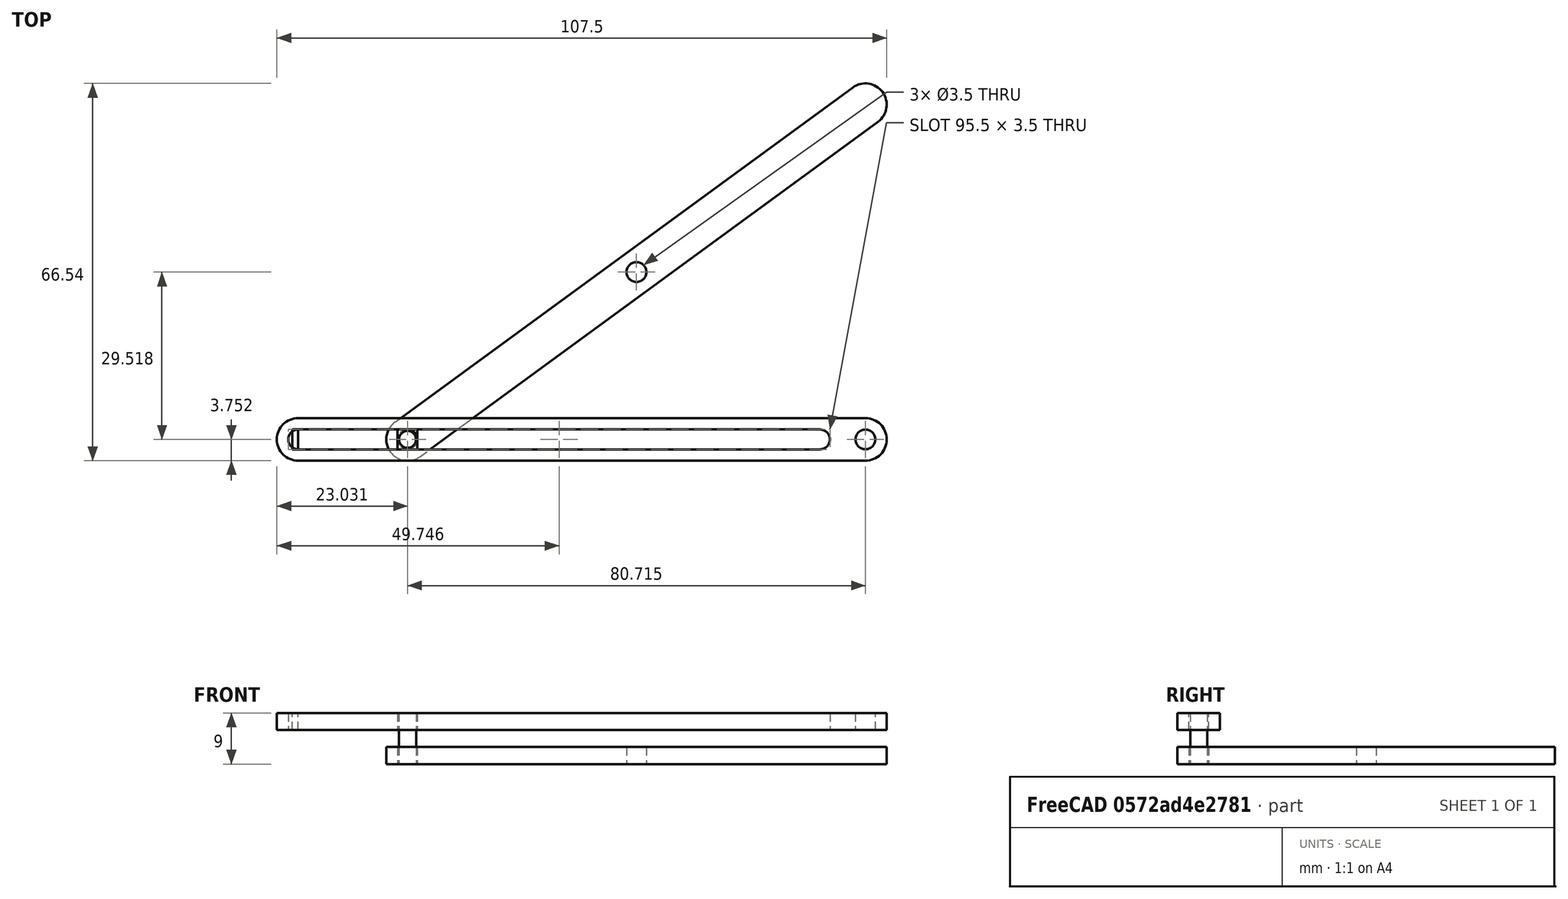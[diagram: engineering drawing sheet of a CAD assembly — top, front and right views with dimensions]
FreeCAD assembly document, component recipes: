
FREECAD ASSEMBLY — COMPONENT RECIPES ("scissor_lift_stops")

This assembly document has 8 components, labeled P0..P7 below (a component is one placed body or linked part). 8 of them carry a construction recipe — the FreeCAD feature program that regenerates the part from scratch, quoted from this document or its linked companion documents; the rest are supplied as boundary geometry only. No exploded tour is included for this assembly.
COMPONENT P0 — recipe-attached ("base", modeled in this document).
Construction recipe (the document's own serialized feature program — sketch geometry with constraints, then the solid features built on it; lengths are millimeters unless a unit is written):

FEATURE [Sketcher::SketchObject] Sketch
  ArcFitTolerance = 1e-06
  AttachmentSupport = -> [XZ_Plane,XY_Plane]
  FullyConstrained = true
  MakeInternals = false
  MapMode = 5
  Placement = pos=(0,0,0) rot=(1,0,0;1.5708rad)
  sketch-geometry (9):
    g0: ArcOfCircle CenterX=-50 CenterY=-4e-16 CenterZ=0 NormalX=0 NormalY=0 NormalZ=1 AngleXU=0 Radius=3.75 StartAngle=1.5708 EndAngle=4.71239
    g1: ArcOfCircle CenterX=50 CenterY=4e-16 CenterZ=0 NormalX=0 NormalY=0 NormalZ=1 AngleXU=0 Radius=3.75 StartAngle=4.71239 EndAngle=7.85398
    g2: LineSegment StartX=-50 StartY=3.75 StartZ=0 EndX=50 EndY=3.75 EndZ=0
    g3: LineSegment StartX=-50 StartY=-3.75 StartZ=0 EndX=50 EndY=-3.75 EndZ=0
    g4: ArcOfCircle CenterX=-50 CenterY=-4e-16 CenterZ=0 NormalX=0 NormalY=0 NormalZ=1 AngleXU=0 Radius=1.75 StartAngle=1.5708 EndAngle=4.71239
    g5: ArcOfCircle CenterX=42 CenterY=0 CenterZ=0 NormalX=0 NormalY=0 NormalZ=1 AngleXU=0 Radius=1.75 StartAngle=4.71239 EndAngle=7.85398
    g6: LineSegment StartX=-50 StartY=1.75 StartZ=0 EndX=42 EndY=1.75 EndZ=0
    g7: LineSegment StartX=-50 StartY=-1.75 StartZ=0 EndX=42 EndY=-1.75 EndZ=0
    g8: Circle CenterX=50 CenterY=4e-16 CenterZ=0 NormalX=0 NormalY=0 NormalZ=1 AngleXU=0 Radius=1.75
  constraints (20):
    c: Tangent(g0,g2) = 1.5708
    c: Tangent(g0,g3) = -1.5708
    c: Tangent(g1,g2) = 1.5708
    c: Tangent(g1,g3) = -1.5708
    c: Equal(g0,g1)
    c: Horizontal(g3)
    c: Tangent(g4,g6) = 1.5708
    c: Tangent(g4,g7) = -1.5708
    c: Tangent(g5,g6) = 1.5708
    c: Tangent(g5,g7) = -1.5708
    c: Equal(g4,g5)
    c: Distance(g4,g4) = 3.5
    c: Coincident(g4,g0)
    c: DistanceX(g0,g1) = 100
    c: Distance(g1,g1) = 7.5
    c: Coincident(g8,g1)
    c: Diameter(g8) = 3.5
    c: Symmetric(g0,g1,g-1)
    c: PointOnObject(g5,g-1)
    c: DistanceX(g5,g1) = 8
FEATURE [PartDesign::Pad] Pad
  Direction = (0,-1,2e-16)
  Length = 3
  Length2 = 10
  Placement = pos=(0,0,0) rot=(1,0,0;1.5708rad)
  Profile = -> Sketch
  ReferenceAxis = -> Sketch [N_Axis]
  Suppressed = false
  Type = 0
FEATURE [PartDesign::Body] Body  label="base"
  AllowCompound = false
  Group = -> [Sketch,Pad]
  Origin = -> Origin
  Placement = pos=(0.39609,-4.19756,1.45633) rot=(1,0,0;4.71239rad)
  Tip = -> Pad
COMPONENT P1 — recipe-attached ("arm_1", modeled in this document).
Construction recipe (the document's own serialized feature program — sketch geometry with constraints, then the solid features built on it; lengths are millimeters unless a unit is written):

FEATURE [PartDesign::SubShapeBinder] Binder
  BindCopyOnChange = 0
  BindMode = 0
  ClaimChildren = false
  Context = -> Assembly [Body001.Binder.]
  Fuse = false
  MakeFace = true
  OffsetFill = false
  OffsetIntersection = false
  OffsetJoinType = 0
  OffsetOpenResult = false
  PartialLoad = false
  Relative = true
  Support = -> [Body]
  _Version = 2
FEATURE [Sketcher::SketchObject] Sketch001
  ArcFitTolerance = 1e-06
  AttachmentSupport = -> [XY_Plane001]
  FullyConstrained = false
  MakeInternals = false
  MapMode = 5
  sketch-geometry (6):
    g0: ArcOfCircle CenterX=-50 CenterY=0 CenterZ=0 NormalX=0 NormalY=0 NormalZ=1 AngleXU=0 Radius=3.75 StartAngle=1.5708 EndAngle=4.71239
    g1: ArcOfCircle CenterX=50 CenterY=-8.2e-15 CenterZ=0 NormalX=0 NormalY=0 NormalZ=1 AngleXU=0 Radius=3.75 StartAngle=4.71239 EndAngle=7.85398
    g2: LineSegment StartX=-50 StartY=3.75 StartZ=0 EndX=50 EndY=3.75 EndZ=0
    g3: LineSegment StartX=-50 StartY=-3.75 StartZ=0 EndX=50 EndY=-3.75 EndZ=0
    g4: Circle CenterX=0 CenterY=0 CenterZ=0 NormalX=0 NormalY=0 NormalZ=1 AngleXU=0 Radius=1.75
    g5: Circle CenterX=-50 CenterY=0 CenterZ=0 NormalX=0 NormalY=0 NormalZ=1 AngleXU=0 Radius=1.75
  constraints (9):
    c: Tangent(g0,g2) = 1.5708
    c: Tangent(g0,g3) = -1.5708
    c: Tangent(g1,g2) = 1.5708
    c: Tangent(g1,g3) = -1.5708
    c: Equal(g0,g1)
    c: Horizontal(g3)
    c: Symmetric(g0,g1,g-1)
    c: Coincident(g4,g-1)
    c: Coincident(g5,g0)
FEATURE [PartDesign::Pad] Pad001
  Direction = (0,0,1)
  Length = 3
  Length2 = 10
  Profile = -> Sketch001
  ReferenceAxis = -> Sketch001 [N_Axis]
  Suppressed = false
  Type = 0
FEATURE [PartDesign::Body] Body001  label="arm_1"
  AllowCompound = false
  Group = -> [Binder,Sketch001,Pad001]
  Origin = -> Origin001
  Placement = pos=(10.0387,25.32,-1.54367) rot=(0,0,1;2.5101rad)
  Tip = -> Pad001
COMPONENT P2 — recipe-attached ("arm_2", modeled in this document).
Construction recipe (the document's own serialized feature program — sketch geometry with constraints, then the solid features built on it; lengths are millimeters unless a unit is written):

FEATURE [PartDesign::FeatureBase] Clone
  BaseFeature = -> Body001
  Placement = pos=(0,18.3,0) rot=(0,0,1;0rad)
  Suppressed = false
FEATURE [PartDesign::Body] Body002  label="arm_2"
  AllowCompound = false
  Group = -> [Clone]
  Origin = -> Origin002
  Placement = pos=(20.8422,10.5492,-4.54367) rot=(0,0,1;0.631493rad)
  Tip = -> Clone
COMPONENT P3 — recipe-attached ("pin_1", modeled in this document).
Construction recipe (the document's own serialized feature program — sketch geometry with constraints, then the solid features built on it; lengths are millimeters unless a unit is written):

FEATURE [Sketcher::SketchObject] Sketch002
  ArcFitTolerance = 1e-06
  AttachmentSupport = -> [XY_Plane003]
  FullyConstrained = true
  MakeInternals = false
  MapMode = 5
  sketch-geometry (1):
    g0: Circle CenterX=0 CenterY=0 CenterZ=0 NormalX=0 NormalY=0 NormalZ=1 AngleXU=0 Radius=1.5
  constraints (2):
    c: Coincident(g0,g-1)
    c: Diameter(g0) = 3
FEATURE [PartDesign::Pad] Pad002
  Direction = (0,0,1)
  Length = 9
  Length2 = 10
  Profile = -> Sketch002
  ReferenceAxis = -> Sketch002 [N_Axis]
  Suppressed = false
  Type = 0
FEATURE [PartDesign::Body] Body003  label="pin_1"
  AllowCompound = false
  Group = -> [Sketch002,Pad002]
  Origin = -> Origin003
  Placement = pos=(50.3961,-4.19756,4.45633) rot=(1,0,0;3.14159rad)
  Tip = -> Pad002
COMPONENT P4 — recipe-attached ("pin_2", modeled in this document).
Construction recipe (the document's own serialized feature program — sketch geometry with constraints, then the solid features built on it; lengths are millimeters unless a unit is written):

FEATURE [PartDesign::FeatureBase] Clone001
  BaseFeature = -> Body003
  Placement = pos=(-22.5,-16.7,0) rot=(0,0,1;0rad)
  Suppressed = false
FEATURE [PartDesign::Body] Body004  label="pin_2"
  AllowCompound = false
  Group = -> [Clone001]
  Origin = -> Origin004
  Placement = pos=(32.6906,8.82653,-6.04367) rot=(0,0,-1;1.26786rad)
  Tip = -> Clone001
COMPONENT P5 — recipe-attached ("pin_3", modeled in this document).
Construction recipe (the document's own serialized feature program — sketch geometry with constraints, then the solid features built on it; lengths are millimeters unless a unit is written):

FEATURE [PartDesign::FeatureBase] Clone002
  BaseFeature = -> Body004
  Suppressed = false
FEATURE [PartDesign::Body] Body005  label="pin_3"
  AllowCompound = false
  Group = -> [Clone002]
  Origin = -> Origin005
  Placement = pos=(-14.6097,19.0053,-4.54367) rot=(0,0,1;0.337153rad)
  Tip = -> Clone002
COMPONENT P6 — recipe-attached ("pin_slider", modeled in this document).
Construction recipe (the document's own serialized feature program — sketch geometry with constraints, then the solid features built on it; lengths are millimeters unless a unit is written):

FEATURE [Sketcher::SketchObject] Sketch003
  ArcFitTolerance = 1e-06
  AttachmentSupport = -> [XY_Plane007]
  FullyConstrained = true
  MakeInternals = false
  MapMode = 5
  sketch-geometry (4):
    g0: LineSegment StartX=-1.75 StartY=1.75 StartZ=0 EndX=-1.75 EndY=-1.75 EndZ=0
    g1: LineSegment StartX=-1.75 StartY=-1.75 StartZ=0 EndX=1.75 EndY=-1.75 EndZ=0
    g2: LineSegment StartX=1.75 StartY=-1.75 StartZ=0 EndX=1.75 EndY=1.75 EndZ=0
    g3: LineSegment StartX=1.75 StartY=1.75 StartZ=0 EndX=-1.75 EndY=1.75 EndZ=0
  constraints (11):
    c: Coincident(g0,g1)
    c: Coincident(g1,g2)
    c: Coincident(g2,g3)
    c: Coincident(g3,g0)
    c: Vertical(g0)
    c: Vertical(g2)
    c: Horizontal(g1)
    c: Horizontal(g3)
    c: DistanceY(g0,g0) = 3.5
    c: Equal(g3,g0)
    c: Symmetric(g0,g1,g-1)
FEATURE [PartDesign::Pad] Pad003
  Direction = (0,0,1)
  Length = 3
  Length2 = 10
  Profile = -> Sketch003
  ReferenceAxis = -> Sketch003 [N_Axis]
  Suppressed = false
  Type = 0
FEATURE [PartDesign::Body] Body006  label="pin_slider"
  AllowCompound = false
  Group = -> [Sketch003,Pad003]
  Origin = -> Origin007
  Placement = pos=(-30.3186,-4.19756,4.45633) rot=(-0.707107,0.707107,0;3.14159rad)
  Tip = -> Pad003
COMPONENT P7 — recipe-attached ("pin_stop", modeled in this document).
Construction recipe (the document's own serialized feature program — sketch geometry with constraints, then the solid features built on it; lengths are millimeters unless a unit is written):

FEATURE [Sketcher::SketchObject] Sketch004
  ArcFitTolerance = 1e-06
  AttachmentSupport = -> [XY_Plane008]
  FullyConstrained = true
  MakeInternals = false
  MapMode = 5
  sketch-geometry (4):
    g0: LineSegment StartX=-1 StartY=1.75 StartZ=0 EndX=-1 EndY=-1.75 EndZ=0
    g1: LineSegment StartX=-1 StartY=-1.75 StartZ=0 EndX=0 EndY=-1.75 EndZ=0
    g2: LineSegment StartX=0 StartY=-1.75 StartZ=0 EndX=0 EndY=1.75 EndZ=0
    g3: LineSegment StartX=0 StartY=1.75 StartZ=0 EndX=-1 EndY=1.75 EndZ=0
  constraints (11):
    c: Coincident(g1,g2)
    c: Coincident(g2,g3)
    c: Coincident(g3,g0)
    c: Vertical(g0)
    c: Vertical(g2)
    c: Horizontal(g1)
    c: Horizontal(g3)
    c: Distance(g0,g0) = 3.5
    c: DistanceX(g3,g3) = 1
    c: Coincident(g0,g1)
    c: Symmetric(g2,g1,g-1)
FEATURE [PartDesign::Pad] Pad004
  Direction = (0,0,1)
  Length = 3
  Length2 = 10
  Profile = -> Sketch004
  ReferenceAxis = -> Sketch004 [N_Axis]
  Suppressed = false
  Type = 0
FEATURE [PartDesign::Body] Body007  label="pin_stop"
  AllowCompound = false
  Group = -> [Sketch004,Pad004]
  Origin = -> Origin008
  Placement = pos=(-49.6039,-4.19756,1.45633) rot=(0,0,1;0rad)
  Tip = -> Pad004
PROVENANCE & LICENSES
A FreeCAD (.FCStd) document from a public repository crawl; recipes are the document's own serialized feature recipes (and, for linked parts, companion documents' recipes).
License: as declared in the source repository (recorded in the dataset sidecar).
